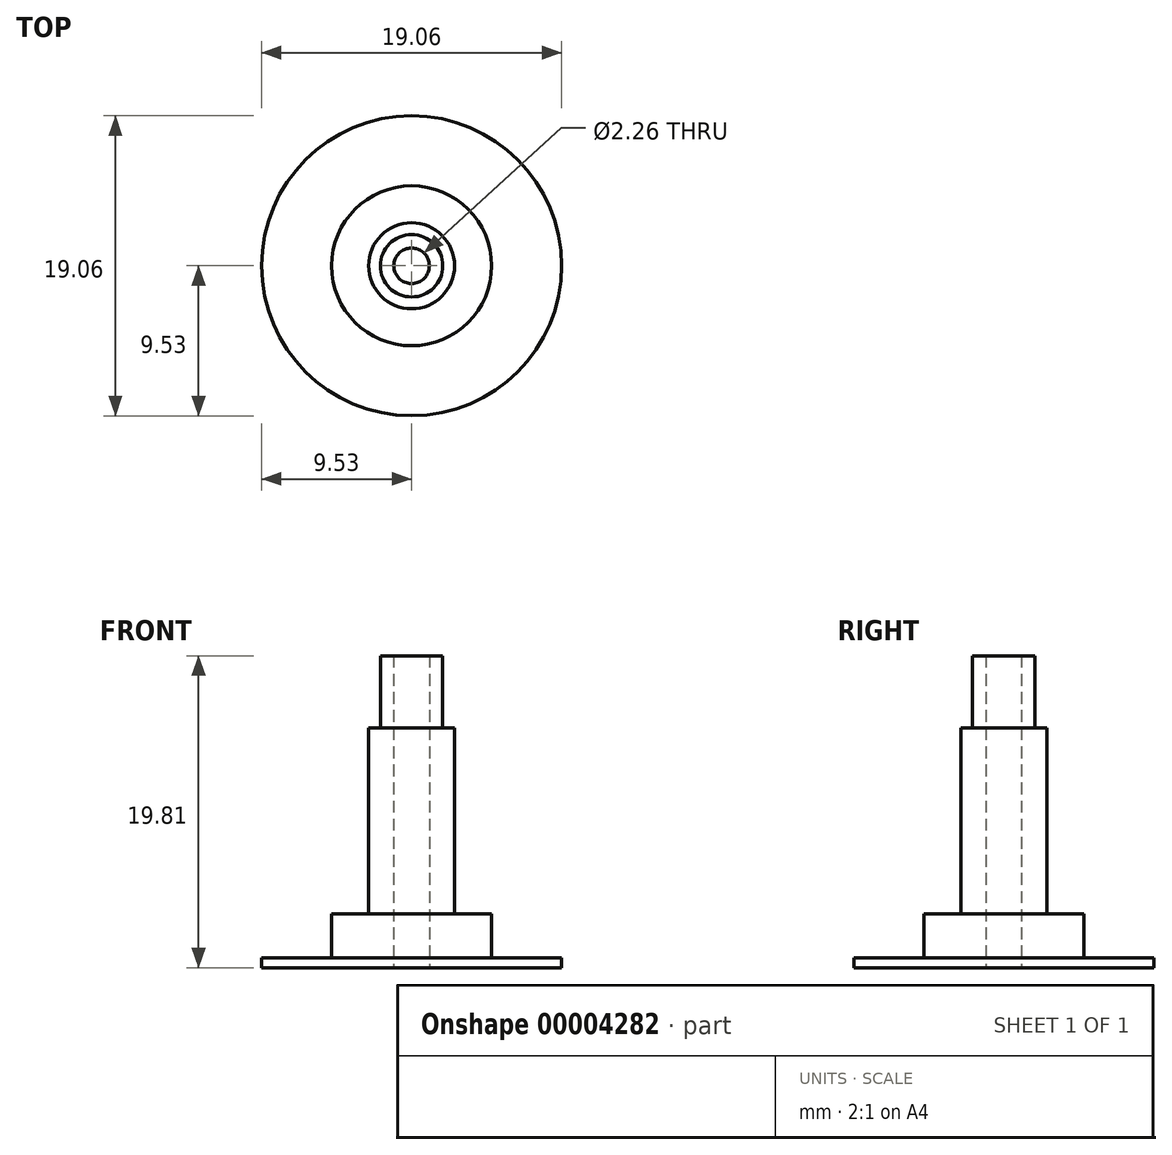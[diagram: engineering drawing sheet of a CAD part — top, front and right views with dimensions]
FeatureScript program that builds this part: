
annotation { "Feature Type Name" : "Feature", "Feature Type Description" : "" }
export const myFeature = defineFeature(function(context is Context, id is Id, definition is map)
    precondition{}
    {
        {
            var Q0;
            Q0=qCreatedBy(makeId("Top.planeOp"),FACE);
            var sketch = newSketch(context, id + "F0", { "sketchPlane" : qUnion([Q0])});
            skCircle(sketch, "E0", {"center": v(0, 0) * mm, "radius": 9.53 * mm});
            skCircle(sketch, "E1", {"center": v(0, 0) * mm, "radius": 5.08 * mm});
            skCircle(sketch, "E2", {"center": v(0, 0) * mm, "radius": 2.73 * mm});
            skCircle(sketch, "E3", {"center": v(0, 0) * mm, "radius": 1.98 * mm});
            skCircle(sketch, "E4", {"center": v(0, 0) * mm, "radius": 1.13 * mm});
            skSolve(sketch);
        }
        {
            var Q0;
            Q0=makeQuery(id+"F0.imprint","IMPRINT",FACE,{"disambiguationData":[TD([[makeQuery(id+"F0.imprint","IMPRINT",EDGE,{"derivedFrom":sQuery(id+"F0.wireOp",EDGE,"E3")}),1.0]])]});
            extrude(context, id + "F1", {"entities" : qUnion([Q0]), "depth" : 19.8 * mm, "offsetDistance" : 25.4 * mm});
        }
        {
            var Q0;
            Q0=makeQuery(id+"F0.imprint","IMPRINT",FACE,{"disambiguationData":[TD([[makeQuery(id+"F0.imprint","IMPRINT",EDGE,{"derivedFrom":sQuery(id+"F0.wireOp",EDGE,"E2")}),1.0]])]});
            extrude(context, id + "F2", {"entities" : qUnion([Q0]), "operationType" : NewBodyOperationType.ADD, "depth" : 15.24 * mm, "offsetDistance" : 25.4 * mm});
        }
        {
            var Q0;
            Q0=makeQuery(id+"F0.imprint","IMPRINT",FACE,{"disambiguationData":[TD([[makeQuery(id+"F0.imprint","IMPRINT",EDGE,{"derivedFrom":sQuery(id+"F0.wireOp",EDGE,"E1")}),1.0]])]});
            extrude(context, id + "F3", {"entities" : qUnion([Q0]), "operationType" : NewBodyOperationType.ADD, "depth" : 3.43 * mm, "offsetDistance" : 25.4 * mm});
        }
        {
            var Q0;
            Q0=makeQuery(id+"F0.imprint","IMPRINT",FACE,{"disambiguationData":[TD([[makeQuery(id+"F0.imprint","IMPRINT",EDGE,{"derivedFrom":sQuery(id+"F0.wireOp",EDGE,"E0")}),1.0]])]});
            extrude(context, id + "F4", {"entities" : qUnion([Q0]), "operationType" : NewBodyOperationType.ADD, "depth" : 0.64 * mm, "offsetDistance" : 25.4 * mm});
        }
    });
